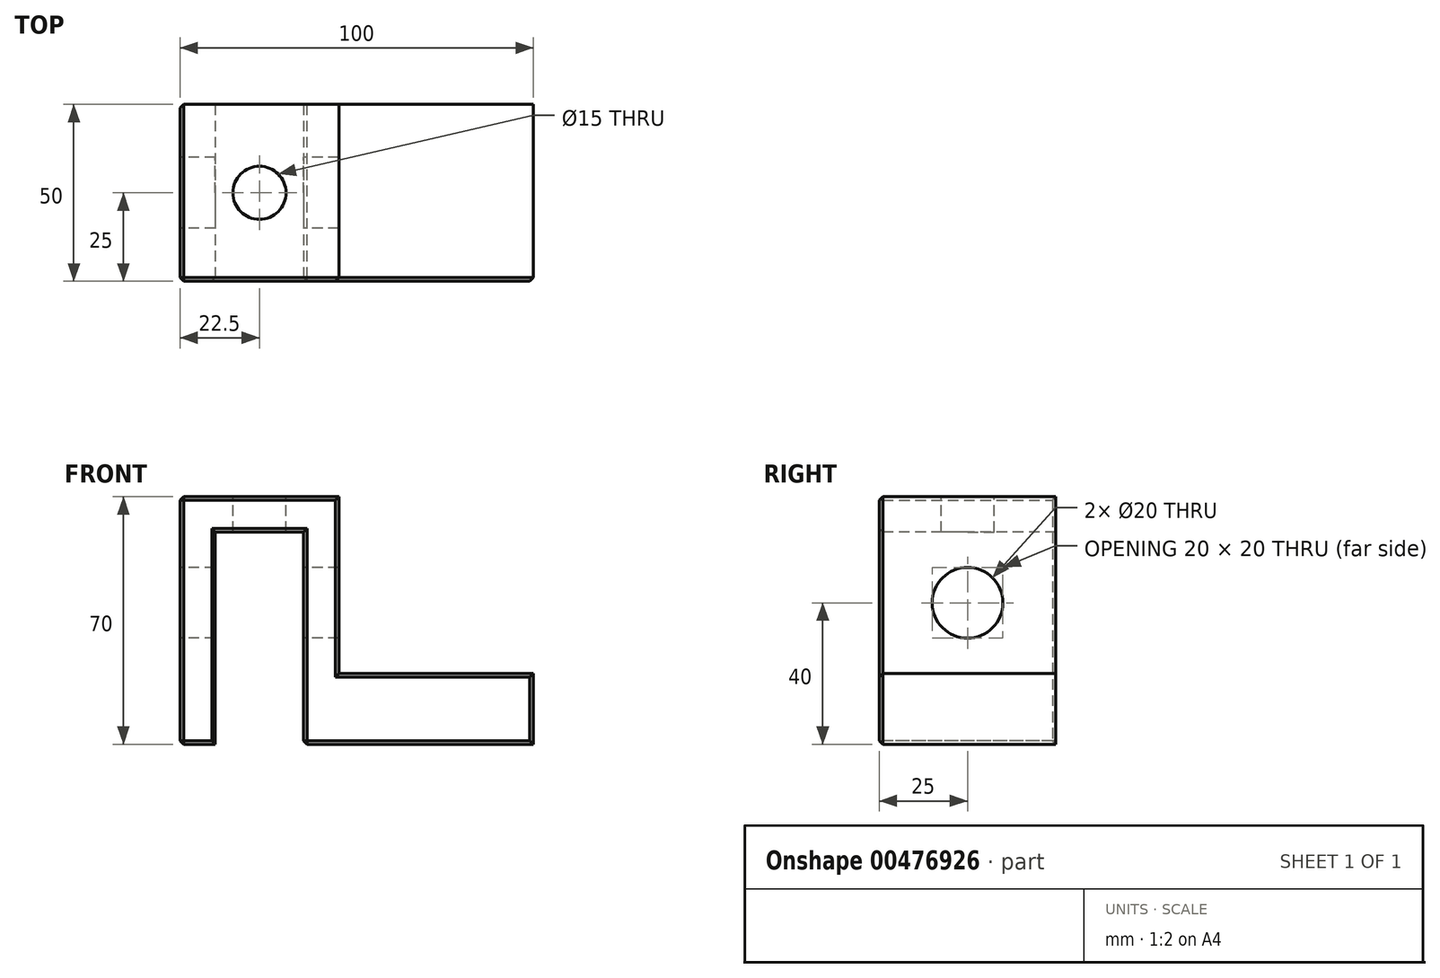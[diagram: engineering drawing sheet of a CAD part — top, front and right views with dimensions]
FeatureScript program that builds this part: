
annotation { "Feature Type Name" : "Feature", "Feature Type Description" : "" }
export const myFeature = defineFeature(function(context is Context, id is Id, definition is map)
    precondition{}
    {
        {
            var Q0;
            Q0=qCreatedBy(makeId("Top.planeOp"),FACE);
            var sketch = newSketch(context, id + "F0", { "sketchPlane" : qUnion([Q0])});
            skLineSegment(sketch, "E0.bottom", {"start": v(0, 0) * mm, "end": v(100, 0) * mm});
            skLineSegment(sketch, "E0.top", {"start": v(0, 50) * mm, "end": v(100, 50) * mm});
            skLineSegment(sketch, "E0.left", {"start": v(0, 0) * mm, "end": v(0, 50) * mm});
            skLineSegment(sketch, "E0.right", {"start": v(100, 0) * mm, "end": v(100, 50) * mm});
            skSolve(sketch);
        }
        {
            var Q0;
            Q0 = qSketchRegion(id + "F0", true);
            extrude(context, id + "F1", {"entities" : qUnion([Q0]), "depth" : 20 * mm});
        }
        {
            var Q0;
            Q0=makeQuery(id+"F1.opExtrude","CAP_FACE",FACE,{"disambiguationData":[OSD([sQuery(id+"F0.wireOp",EDGE,"E0.bottom"),sQuery(id+"F0.wireOp",EDGE,"E0.top"),sQuery(id+"F0.wireOp",EDGE,"E0.left"),sQuery(id+"F0.wireOp",EDGE,"E0.right")])],"isStart":false});
            var sketch = newSketch(context, id + "F2", { "sketchPlane" : qUnion([Q0])});
            skLineSegment(sketch, "E1.bottom", {"start": v(0, 0) * mm, "end": v(45, 0) * mm});
            skLineSegment(sketch, "E1.top", {"start": v(0, 50) * mm, "end": v(45, 50) * mm});
            skLineSegment(sketch, "E1.left", {"start": v(0, 0) * mm, "end": v(0, 50) * mm});
            skLineSegment(sketch, "E1.right", {"start": v(45, 0) * mm, "end": v(45, 50) * mm});
            skSolve(sketch);
        }
        {
            var Q0;
            Q0 = qSketchRegion(id + "F2", true);
            extrude(context, id + "F3", {"entities" : qUnion([Q0]), "operationType" : NewBodyOperationType.ADD, "depth" : 50 * mm});
        }
        {
            var Q0;
            Q0=makeQuery(id+"F3.boolean.opBoolean","MERGE",FACE,{"derivedFrom":[makeQuery(id+"F1.opExtrude","SWEPT_FACE",FACE,{"disambiguationData":[OSD([sQuery(id+"F0.wireOp",EDGE,"E0.bottom")])]}),makeQuery(id+"F3.opExtrude","SWEPT_FACE",FACE,{"disambiguationData":[OSD([sQuery(id+"F2.wireOp",EDGE,"E1.bottom")])]})]});
            var sketch = newSketch(context, id + "F4", { "sketchPlane" : qUnion([Q0])});
            skLineSegment(sketch, "E2.bottom", {"start": v(10, 0) * mm, "end": v(35, 0) * mm});
            skLineSegment(sketch, "E2.top", {"start": v(10, 60) * mm, "end": v(35, 60) * mm});
            skLineSegment(sketch, "E2.left", {"start": v(10, 0) * mm, "end": v(10, 60) * mm});
            skLineSegment(sketch, "E2.right", {"start": v(35, 0) * mm, "end": v(35, 60) * mm});
            skSolve(sketch);
        }
        {
            var Q0;
            Q0 = qSketchRegion(id + "F4", true);
            extrude(context, id + "F5", {"entities" : qUnion([Q0]), "operationType" : NewBodyOperationType.REMOVE, "endBound" : BoundingType.THROUGH_ALL, "oppositeDirection" : true, "depth" : 25 * mm});
        }
        {
            var Q0;
            Q0=makeQuery(id+"F3.boolean.opBoolean","MERGE",FACE,{"derivedFrom":[makeQuery(id+"F1.opExtrude","SWEPT_FACE",FACE,{"disambiguationData":[OSD([sQuery(id+"F0.wireOp",EDGE,"E0.left")])]}),makeQuery(id+"F3.opExtrude","SWEPT_FACE",FACE,{"disambiguationData":[OSD([sQuery(id+"F2.wireOp",EDGE,"E1.left")])]})]});
            var sketch = newSketch(context, id + "F6", { "sketchPlane" : qUnion([Q0])});
            skCircle(sketch, "E3", {"center": v(-25, 40) * mm, "radius": 10 * mm});
            skSolve(sketch);
        }
        {
            var Q0;
            Q0 = qSketchRegion(id + "F6", true);
            extrude(context, id + "F7", {"entities" : qUnion([Q0]), "operationType" : NewBodyOperationType.REMOVE, "endBound" : BoundingType.THROUGH_ALL, "oppositeDirection" : true, "depth" : 25 * mm});
        }
        {
            var Q0;
            Q0=makeQuery(id+"F3.opExtrude","CAP_FACE",FACE,{"disambiguationData":[OSD([sQuery(id+"F2.wireOp",EDGE,"E1.bottom"),sQuery(id+"F2.wireOp",EDGE,"E1.top"),sQuery(id+"F2.wireOp",EDGE,"E1.left"),sQuery(id+"F2.wireOp",EDGE,"E1.right")])],"isStart":false});
            var sketch = newSketch(context, id + "F8", { "sketchPlane" : qUnion([Q0])});
            skLineSegment(sketch, "E4", {"start": v(0, 50) * mm, "end": v(45, 0) * mm, "construction": true});
            skLineSegment(sketch, "E5", {"start": v(45, 0) * mm, "end": v(45, 50) * mm, "construction": true});
            skLineSegment(sketch, "E6", {"start": v(45, 50) * mm, "end": v(0, 0) * mm, "construction": true});
            skCircle(sketch, "E7", {"center": v(22.5, 25) * mm, "radius": 7.5 * mm});
            skSolve(sketch);
        }
        {
            var Q0;
            Q0=makeQuery(id+"F8.imprint","IMPRINT",FACE,{"disambiguationData":[TD([[makeQuery(id+"F8.imprint","IMPRINT",EDGE,{"derivedFrom":sQuery(id+"F8.wireOp",EDGE,"E7")}),-1.0]])]});
            var sketch = newSketch(context, id + "F9", { "sketchPlane" : qUnion([Q0])});
            skSolve(sketch);
        }
        {
            var Q0;
            Q0 = qSketchRegion(id + "F9", true);
            var Q1;
            Q1=makeQuery(id+"F8.imprint","IMPRINT",FACE,{"disambiguationData":[TD([[makeQuery(id+"F8.imprint","IMPRINT",EDGE,{"derivedFrom":sQuery(id+"F8.wireOp",EDGE,"E7")}),1.0]])]});
            extrude(context, id + "F10", {"entities" : qUnion([Q0, Q1]), "operationType" : NewBodyOperationType.REMOVE, "endBound" : BoundingType.THROUGH_ALL, "oppositeDirection" : true, "depth" : 25 * mm});
        }
        {
            var Q0;
            Q0=makeQuery(id+"F3.opExtrude","CAP_EDGE",EDGE,{"disambiguationData":[OSD([sQuery(id+"F2.wireOp",EDGE,"E1.left")])],"isStart":false});
            var Q1;
            Q1=makeQuery(id+"F3.boolean.opBoolean","MERGE",EDGE,{"derivedFrom":[makeQuery(id+"F1.opExtrude","SWEPT_EDGE",EDGE,{"disambiguationData":[OSD([sQuery(id+"F0.wireOp",EDGE,"E0.top"),sQuery(id+"F0.wireOp",EDGE,"E0.left")])]}),makeQuery(id+"F3.opExtrude","SWEPT_EDGE",EDGE,{"disambiguationData":[OSD([sQuery(id+"F2.wireOp",EDGE,"E1.top"),sQuery(id+"F2.wireOp",EDGE,"E1.left")])]})]});
            var Q2;
            Q2=makeQuery(id+"F1.opExtrude","CAP_EDGE",EDGE,{"disambiguationData":[OSD([sQuery(id+"F0.wireOp",EDGE,"E0.left")])],"isStart":true});
            var Q3;
            Q3=makeQuery(id+"F5.boolean.opBoolean","COPY",EDGE,{"derivedFrom":makeQuery(id+"F5.opExtrude","CAP_EDGE",EDGE,{"disambiguationData":[OSD([sQuery(id+"F4.wireOp",EDGE,"E2.left")])],"isStart":true})});
            var Q4;
            {var subQ0=sQuery(id+"F0.wireOp",EDGE,"E0.left");var subQ1=sQuery(id+"F0.wireOp",EDGE,"E0.bottom");Q4=makeQuery(id+"F5.boolean.opBoolean","SPLIT",EDGE,{"disambiguationData":[TD([makeQuery(id+"F1.opExtrude","SWEPT_FACE",FACE,{"disambiguationData":[OSD([subQ0])]})])],"derivedFrom":makeQuery(id+"F1.opExtrude","CAP_EDGE",EDGE,{"disambiguationData":[OSD([subQ1])],"isStart":true})});}
            var Q5;
            Q5=makeQuery(id+"F5.boolean.opBoolean","COPY",EDGE,{"derivedFrom":makeQuery(id+"F5.opExtrude","CAP_EDGE",EDGE,{"disambiguationData":[OSD([sQuery(id+"F4.wireOp",EDGE,"E2.top")])],"isStart":true})});
            var Q6;
            Q6=makeQuery(id+"F5.boolean.opBoolean","COPY",EDGE,{"derivedFrom":makeQuery(id+"F5.opExtrude","CAP_EDGE",EDGE,{"disambiguationData":[OSD([sQuery(id+"F4.wireOp",EDGE,"E2.right")])],"isStart":true})});
            var Q7;
            Q7=makeQuery(id+"F5.boolean.opBoolean","COPY",EDGE,{"derivedFrom":makeQuery(id+"F5.opExtrude","SWEPT_EDGE",EDGE,{"disambiguationData":[OSD([sQuery(id+"F0.wireOp",EDGE,"E0.bottom"),sQuery(id+"F4.wireOp",EDGE,"E2.bottom"),sQuery(id+"F4.wireOp",EDGE,"E2.right")])]})});
            var Q8;
            Q8=makeQuery(id+"F3.opExtrude","SWEPT_EDGE",EDGE,{"disambiguationData":[OSD([sQuery(id+"F0.wireOp",EDGE,"E0.bottom"),sQuery(id+"F2.wireOp",EDGE,"E1.bottom"),sQuery(id+"F2.wireOp",EDGE,"E1.right")])]});
            var Q9;
            Q9=makeQuery(id+"F3.boolean.opBoolean","MERGE",FACE,{"derivedFrom":[makeQuery(id+"F1.opExtrude","SWEPT_FACE",FACE,{"disambiguationData":[OSD([sQuery(id+"F0.wireOp",EDGE,"E0.bottom")])]}),makeQuery(id+"F3.opExtrude","SWEPT_FACE",FACE,{"disambiguationData":[OSD([sQuery(id+"F2.wireOp",EDGE,"E1.bottom")])]})]});
            var Q10;
            Q10=makeQuery(id+"F3.boolean.opBoolean","MERGE",EDGE,{"derivedFrom":[makeQuery(id+"F1.opExtrude","SWEPT_EDGE",EDGE,{"disambiguationData":[OSD([sQuery(id+"F0.wireOp",EDGE,"E0.bottom"),sQuery(id+"F0.wireOp",EDGE,"E0.left")])]}),makeQuery(id+"F3.opExtrude","SWEPT_EDGE",EDGE,{"disambiguationData":[OSD([sQuery(id+"F2.wireOp",EDGE,"E1.bottom"),sQuery(id+"F2.wireOp",EDGE,"E1.left")])]})]});
            chamfer(context, id + "F11", {"entities" : qUnion([Q0, Q1, Q2, Q3, Q4, Q5, Q6, Q7, Q8, Q9, Q10]), "width" : 1 * mm, "tangentPropagation" : true});
        }
    });
